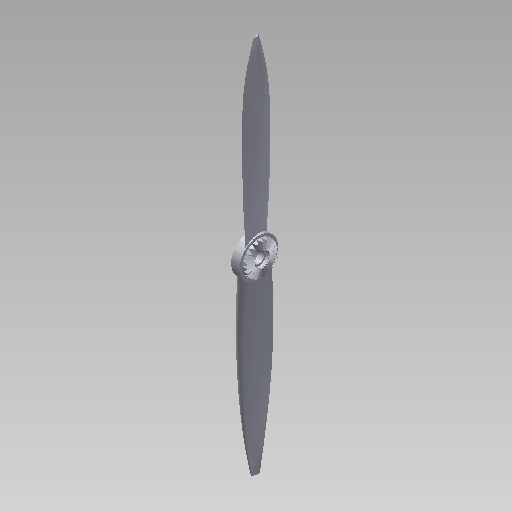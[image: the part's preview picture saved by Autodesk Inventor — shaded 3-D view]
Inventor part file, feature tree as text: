
AUTODESK INVENTOR PART (.ipt)
format: ipt  version: 2018.1 (Build 221171000, 171)  size: 472,064 bytes
history: native  units: in
note: dims shown in document units (in); Inventor stores cm internally (conversion verified against a paired STEP export)
features: sketch x6, extrude x5, plane x5, pattern_circular x2, revolve x1, loft x1, other x1
ambient origin geometry x8: Origin, YZ Plane, XZ Plane, XY Plane, X Axis, Y Axis, Z Axis, Center Point
bodies: Solid1 (feature_tree)
feature tree (21):
  revolve  "Revolution1"  [1 undecoded]
  extrude  "Extrusion2"  Depth=0.2047in
  pattern_circular  "Circular Pattern1"  [2 undecoded]
  extrude  "Extrusion3"  Depth=0.0787in TaperAngle=0.0deg
  plane  "Work Plane2"
  extrude  "Extrusion4"  Depth=0.0787in
  plane  "Work Plane3"
  extrude  "Extrusion5"  Depth=0.0787in TaperAngle=360.0deg
  plane  "Work Plane6"
  plane  "Work Plane8"
  plane  "Work Plane9"
  loft  "Loft3"
  pattern_circular  "Circular Pattern3"  Angle=90.0deg  [1 undecoded]
  extrude  "Extrusion6"  [1 undecoded]
  sketch  "Sketch1"  dims[d5=90.0deg d12=0.0787in d13=-0.1787in]
  sketch  "Sketch3"  dims[d14=9.0551in d15=360.0deg d17=0.2047in]
  sketch  "Sketch4"  dims[d18=0.3937in d19=0.0in]
  sketch  "Sketch5"  dims[d20=0.2362in]
  sketch  "Sketch6"  dims[d21=0.2756in]
  sketch  "Sketch11"  dims[d22=0.0787in d23=0.0in d26=0.3543in d27=0.1969in d28=0.0in d31=1.2598in d33=2.5197in d34=3.1496in d54=0.7874in d55=360.0deg d58=0.1969in d59=0.0in d66=0.0in d67=90.0deg d68=0.0in d69=90.0deg d70=0.0in d71=90.0deg d72=0.0in d73=90.0deg]
  other  "Edges4"
note: 5 required parameter values undecoded (feature->parameter linkage not recoverable at this tier; creation-order binding heuristic only, values carry confidence <= 0.55)